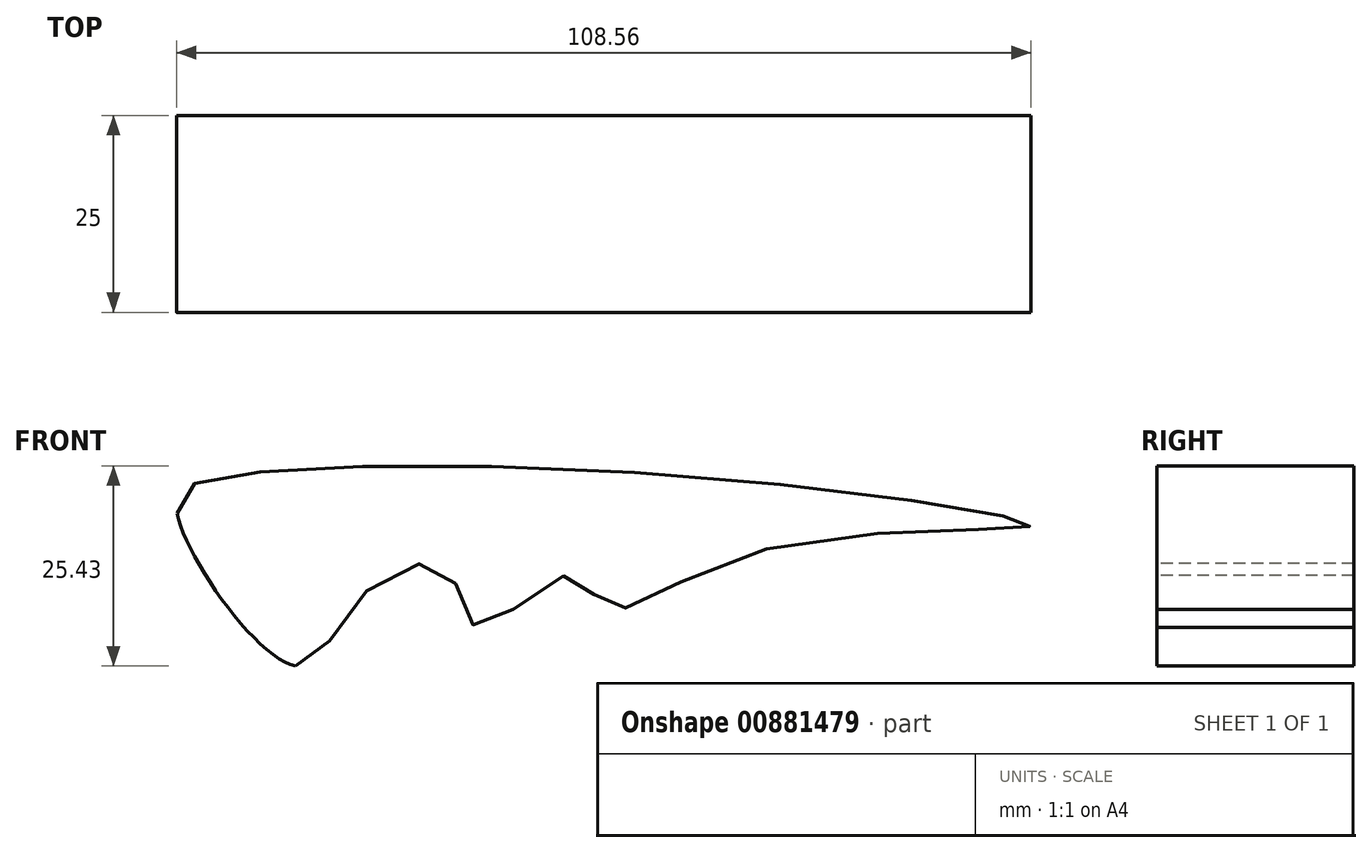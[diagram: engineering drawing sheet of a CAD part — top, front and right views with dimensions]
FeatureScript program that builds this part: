
annotation { "Feature Type Name" : "Feature", "Feature Type Description" : "" }
export const myFeature = defineFeature(function(context is Context, id is Id, definition is map)
    precondition{}
    {
        {
            var Q0;
            Q0=qCreatedBy(makeId("Front.planeOp"),FACE);
            var sketch = newSketch(context, id + "F0", { "sketchPlane" : qUnion([Q0])});
            skFitSpline(sketch, "E0", {"points": [v(-65.9, 0) * mm, v(0, 0) * mm, v(38.3, -5.93) * mm, v(2.77, -9.4) * mm, v(-15.48, -16.22) * mm, v(-20.27, -12.16) * mm, v(-31.83, -18.8) * mm, v(-35.82, -11.58) * mm, v(-47, -15.17) * mm, v(-55.03, -23.66) * mm, v(-70.07, -4.3) * mm, v(-65.9, 0) * mm]});
            skLineSegment(sketch, "E1", {"start": v(-70.07, -4.3) * mm, "end": v(-70.07, -24.3) * mm});
            skLineSegment(sketch, "E2", {"start": v(-70.07, -24.3) * mm, "end": v(-55.03, -23.66) * mm});
            skSolve(sketch);
        }
        {
            var Q0;
            Q0=makeQuery(id+"F0.imprint","IMPRINT",FACE,{"disambiguationData":[TD([[makeQuery(id+"F0.imprint","IMPRINT",EDGE,{"derivedFrom":sQuery(id+"F0.wireOp",EDGE,"E0")}),-1.0]])]});
            extrude(context, id + "F1", {"entities" : qUnion([Q0]), "depth" : 25 * mm, "offsetDistance" : 25 * mm});
        }
    });
